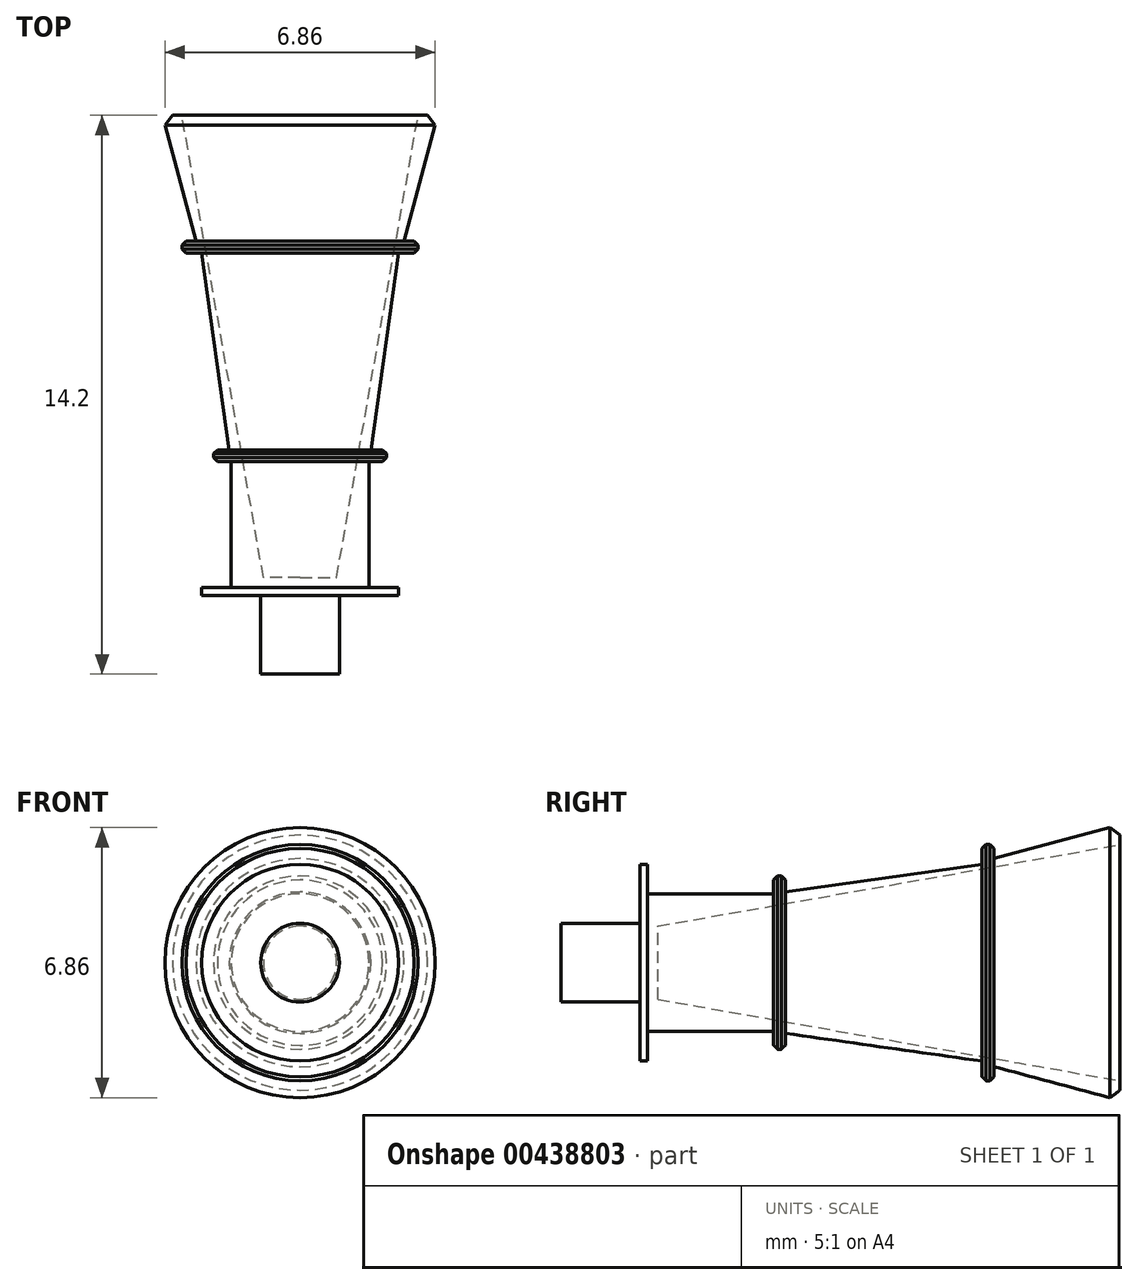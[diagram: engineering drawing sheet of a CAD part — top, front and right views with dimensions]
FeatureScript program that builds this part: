
annotation { "Feature Type Name" : "Feature", "Feature Type Description" : "" }
export const myFeature = defineFeature(function(context is Context, id is Id, definition is map)
    precondition{}
    {
        {
            var Q0;
            Q0=qCreatedBy(makeId("Front.planeOp"),FACE);
            var sketch = newSketch(context, id + "F0", { "sketchPlane" : qUnion([Q0])});
            skCircle(sketch, "E0", {"center": v(0, 0) * mm, "radius": 3.5 * mm});
            skSolve(sketch);
        }
        {
            var Q0;
            Q0 = qSketchRegion(id + "F0", true);
            extrude(context, id + "F1", {"entities" : qUnion([Q0]), "depth" : 3.2 * mm, "hasDraft" : true, "draftAngle" : 15 * degree, "draftPullDirection" : true});
        }
        {
            var Q0;
            Q0=makeQuery(id+"F1.opExtrude","CAP_FACE",FACE,{"disambiguationData":[OSD([sQuery(id+"F0.wireOp",EDGE,"E0")])],"isStart":false});
            var sketch = newSketch(context, id + "F2", { "sketchPlane" : qUnion([Q0])});
            skCircle(sketch, "E1", {"center": v(0, 0) * mm, "radius": 3 * mm});
            skSolve(sketch);
        }
        {
            var Q0;
            Q0 = qSketchRegion(id + "F2", true);
            extrude(context, id + "F3", {"entities" : qUnion([Q0]), "operationType" : NewBodyOperationType.ADD, "depth" : .3 * mm});
        }
        {
            var Q0;
            Q0=makeQuery(id+"F1.opExtrude","CAP_EDGE",EDGE,{"disambiguationData":[OSD([sQuery(id+"F0.wireOp",EDGE,"E0")])],"isStart":true});
            chamfer(context, id + "F4", {"entities" : qUnion([Q0]), "width" : .2 * mm, "tangentPropagation" : true});
        }
        {
            var Q0;
            Q0=makeQuery(id+"F3.opExtrude","CAP_FACE",FACE,{"disambiguationData":[OSD([sQuery(id+"F2.wireOp",EDGE,"E1")])],"isStart":false});
            var sketch = newSketch(context, id + "F5", { "sketchPlane" : qUnion([Q0])});
            skCircle(sketch, "E2", {"center": v(0, 0) * mm, "radius": 2.5 * mm});
            skSolve(sketch);
        }
        {
            var Q0;
            Q0=makeQuery(id+"F5.imprint","IMPRINT",FACE,{"disambiguationData":[TD([[makeQuery(id+"F5.imprint","IMPRINT",EDGE,{"derivedFrom":sQuery(id+"F5.wireOp",EDGE,"E2")}),1.0]])]});
            extrude(context, id + "F6", {"entities" : qUnion([Q0]), "operationType" : NewBodyOperationType.ADD, "depth" : 5 * mm, "hasDraft" : true, "draftAngle" : 8 * degree, "draftPullDirection" : true});
        }
        {
            var Q0;
            Q0=makeQuery(id+"F6.opExtrude","CAP_FACE",FACE,{"disambiguationData":[OSD([sQuery(id+"F5.wireOp",EDGE,"E2")])],"isStart":false});
            var sketch = newSketch(context, id + "F7", { "sketchPlane" : qUnion([Q0])});
            skCircle(sketch, "E3", {"center": v(0, 0) * mm, "radius": 2.2 * mm});
            skSolve(sketch);
        }
        {
            var Q0;
            Q0 = qSketchRegion(id + "F7", true);
            extrude(context, id + "F8", {"entities" : qUnion([Q0]), "operationType" : NewBodyOperationType.ADD, "depth" : .3 * mm});
        }
        {
            var Q0;
            Q0=makeQuery(id+"F8.opExtrude","CAP_FACE",FACE,{"disambiguationData":[OSD([sQuery(id+"F7.wireOp",EDGE,"E3")])],"isStart":false});
            var sketch = newSketch(context, id + "F9", { "sketchPlane" : qUnion([Q0])});
            skCircle(sketch, "E4", {"center": v(0, 0) * mm, "radius": 1.75 * mm});
            skSolve(sketch);
        }
        {
            var Q0;
            Q0 = qSketchRegion(id + "F9", true);
            extrude(context, id + "F10", {"entities" : qUnion([Q0]), "operationType" : NewBodyOperationType.ADD, "depth" : 3.2 * mm});
        }
        {
            var Q0;
            Q0=makeQuery(id+"F10.opExtrude","CAP_FACE",FACE,{"disambiguationData":[OSD([sQuery(id+"F9.wireOp",EDGE,"E4")])],"isStart":false});
            var sketch = newSketch(context, id + "F11", { "sketchPlane" : qUnion([Q0])});
            skCircle(sketch, "E5", {"center": v(0, 0) * mm, "radius": 2.5 * mm});
            skSolve(sketch);
        }
        {
            var Q0;
            Q0 = qSketchRegion(id + "F11", true);
            extrude(context, id + "F12", {"entities" : qUnion([Q0]), "operationType" : NewBodyOperationType.ADD, "depth" : .2 * mm});
        }
        {
            var Q0;
            Q0=makeQuery(id+"F12.opExtrude","CAP_FACE",FACE,{"disambiguationData":[OSD([sQuery(id+"F11.wireOp",EDGE,"E5")])],"isStart":false});
            var sketch = newSketch(context, id + "F13", { "sketchPlane" : qUnion([Q0])});
            skCircle(sketch, "E6", {"center": v(0, 0) * mm, "radius": 1 * mm});
            skSolve(sketch);
        }
        {
            var Q0;
            Q0 = qSketchRegion(id + "F13", true);
            extrude(context, id + "F14", {"entities" : qUnion([Q0]), "operationType" : NewBodyOperationType.ADD, "depth" : 2 * mm});
        }
        {
            var Q0;
            Q0=makeQuery(id+"F3.opExtrude","CAP_EDGE",EDGE,{"disambiguationData":[OSD([sQuery(id+"F2.wireOp",EDGE,"E1")])],"isStart":false});
            var Q1;
            Q1=makeQuery(id+"F8.opExtrude","CAP_EDGE",EDGE,{"disambiguationData":[OSD([sQuery(id+"F7.wireOp",EDGE,"E3")])],"isStart":false});
            var Q2;
            Q2=makeQuery(id+"F8.opExtrude","CAP_EDGE",EDGE,{"disambiguationData":[OSD([sQuery(id+"F7.wireOp",EDGE,"E3")])],"isStart":true});
            var Q3;
            Q3=makeQuery(id+"F3.opExtrude","CAP_EDGE",EDGE,{"disambiguationData":[OSD([sQuery(id+"F2.wireOp",EDGE,"E1")])],"isStart":true});
            chamfer(context, id + "F15", {"entities" : qUnion([Q0, Q1, Q2, Q3]), "width" : .1 * mm, "tangentPropagation" : true});
        }
        {
            var Q0;
            Q0=makeQuery(id+"F1.opExtrude","CAP_FACE",FACE,{"disambiguationData":[OSD([sQuery(id+"F0.wireOp",EDGE,"E0")])],"isStart":true});
            var sketch = newSketch(context, id + "F16", { "sketchPlane" : qUnion([Q0])});
            skCircle(sketch, "E7", {"center": v(0, 0) * mm, "radius": 3 * mm});
            skSolve(sketch);
        }
        {
            var Q0;
            Q0 = qSketchRegion(id + "F16", true);
            extrude(context, id + "F17", {"entities" : qUnion([Q0]), "operationType" : NewBodyOperationType.REMOVE, "oppositeDirection" : true, "depth" : 23.48 * mm, "hasDraft" : true, "draftAngle" : 10 * degree, "draftPullDirection" : true, "symmetric" : true});
        }
    });
